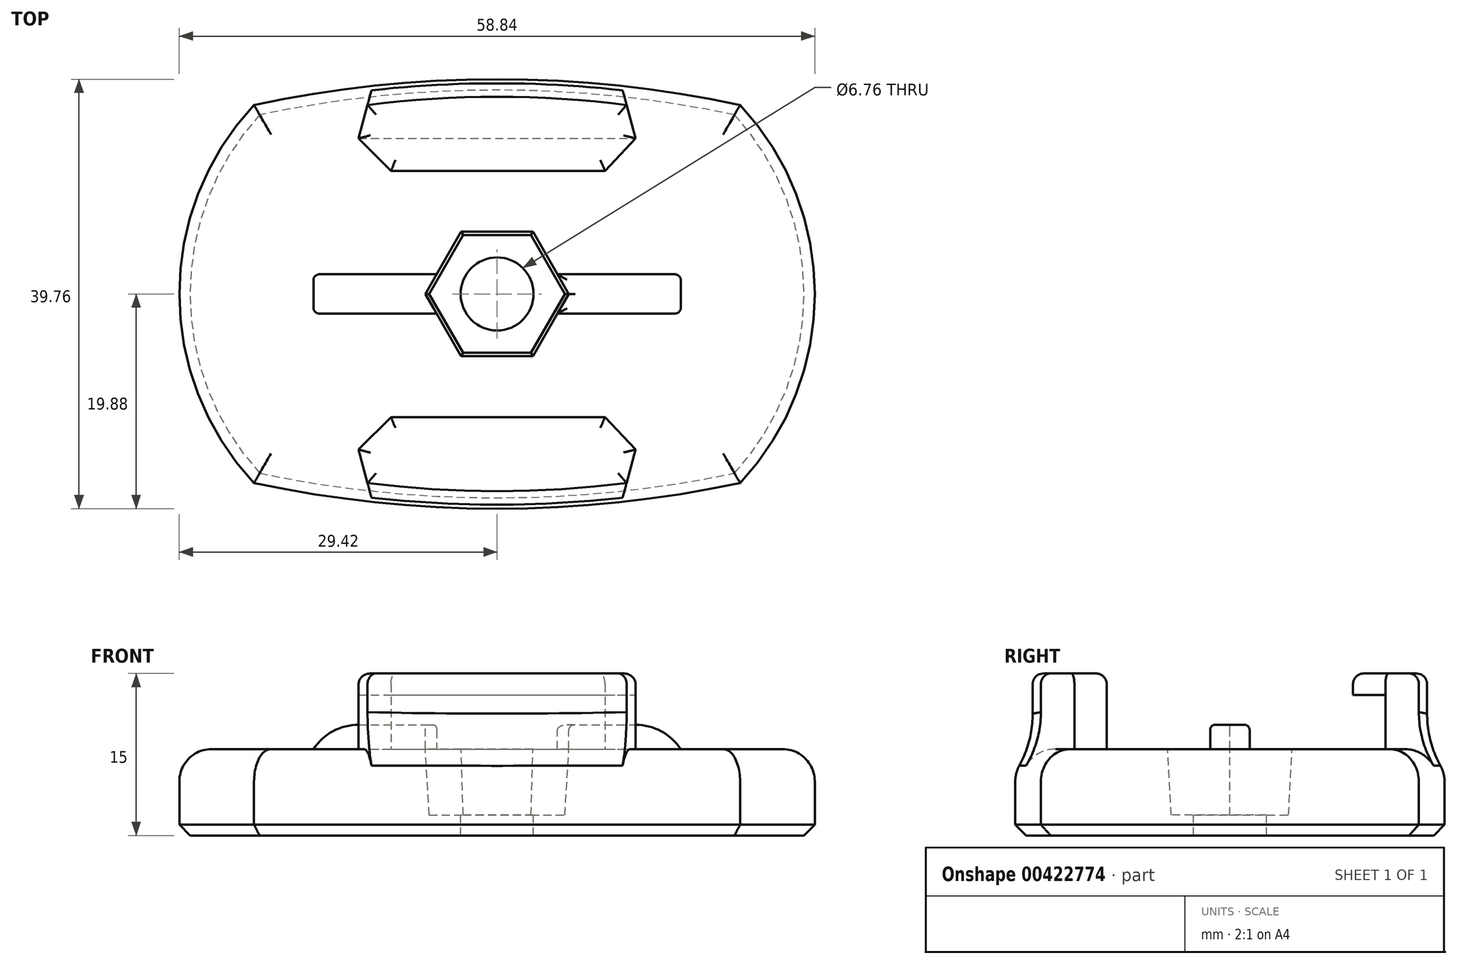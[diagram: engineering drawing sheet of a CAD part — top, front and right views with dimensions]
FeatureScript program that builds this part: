
annotation { "Feature Type Name" : "Feature", "Feature Type Description" : "" }
export const myFeature = defineFeature(function(context is Context, id is Id, definition is map)
    precondition{}
    {
        {
            var Q0;
            Q0=qCreatedBy(makeId("Top.planeOp"),FACE);
            var sketch = newSketch(context, id + "F0", { "sketchPlane" : qUnion([Q0])});
            skLineSegment(sketch, "E0.rect.bottom", {"start": v(-22.5, 17.5) * mm, "end": v(22.5, 17.5) * mm});
            skLineSegment(sketch, "E0.rect.top", {"start": v(-22.5, -17.5) * mm, "end": v(22.5, -17.5) * mm});
            skLineSegment(sketch, "E0.rect.left", {"start": v(-22.5, 17.5) * mm, "end": v(-22.5, -17.5) * mm});
            skLineSegment(sketch, "E0.rect.right", {"start": v(22.5, 17.5) * mm, "end": v(22.5, -17.5) * mm});
            skPoint(sketch, "E0.rect.middle", {"position": v(0, 0) * mm});
            skArc(sketch, "E1", {"start": v(-22.5, 17.5) * mm, "mid": v(-29.42, 0) * mm, "end": v(-22.5, -17.5) * mm});
            skArc(sketch, "E2.MirrorCS", {"start": v(22.5, 17.5) * mm, "mid": v(29.42, 0) * mm, "end": v(22.5, -17.5) * mm});
            skArc(sketch, "E3", {"start": v(22.5, 17.5) * mm, "mid": v(0, 19.88) * mm, "end": v(-22.5, 17.5) * mm});
            skArc(sketch, "E4.MirrorCS", {"start": v(22.5, -17.5) * mm, "mid": v(0, -19.88) * mm, "end": v(-22.5, -17.5) * mm});
            skSolve(sketch);
        }
        {
            var Q0;
            Q0=makeQuery(id+"F0.imprint","IMPRINT",FACE,{"disambiguationData":[TD([[makeQuery(id+"F0.imprint","IMPRINT",EDGE,{"derivedFrom":sQuery(id+"F0.wireOp",EDGE,"E0.rect.bottom")}),-1.0]])]});
            var Q1;
            Q1=makeQuery(id+"F0.imprint","IMPRINT",FACE,{"disambiguationData":[TD([[makeQuery(id+"F0.imprint","IMPRINT",EDGE,{"derivedFrom":sQuery(id+"F0.wireOp",EDGE,"E0.rect.left")}),-1.0]])]});
            var Q2;
            Q2=makeQuery(id+"F0.imprint","IMPRINT",FACE,{"disambiguationData":[TD([[makeQuery(id+"F0.imprint","IMPRINT",EDGE,{"derivedFrom":sQuery(id+"F0.wireOp",EDGE,"E0.rect.right")}),1.0]])]});
            var Q3;
            Q3=makeQuery(id+"F0.imprint","IMPRINT",FACE,{"disambiguationData":[TD([[makeQuery(id+"F0.imprint","IMPRINT",EDGE,{"derivedFrom":sQuery(id+"F0.wireOp",EDGE,"E0.rect.bottom")}),1.0]])]});
            var Q4;
            Q4=makeQuery(id+"F0.imprint","IMPRINT",FACE,{"disambiguationData":[TD([[makeQuery(id+"F0.imprint","IMPRINT",EDGE,{"derivedFrom":sQuery(id+"F0.wireOp",EDGE,"E0.rect.top")}),-1.0]])]});
            extrude(context, id + "F1", {"entities" : qUnion([Q0, Q1, Q2, Q3, Q4]), "depth" : 8 * mm});
        }
        {
            var Q0;
            Q0=makeQuery(id+"F1.opExtrude","CAP_FACE",FACE,{"disambiguationData":[OSD([sQuery(id+"F0.wireOp",EDGE,"E1"),sQuery(id+"F0.wireOp",EDGE,"E2.MirrorCS"),sQuery(id+"F0.wireOp",EDGE,"E3"),sQuery(id+"F0.wireOp",EDGE,"E4.MirrorCS")])],"isStart":false});
            var sketch = newSketch(context, id + "F2", { "sketchPlane" : qUnion([Q0])});
            skLineSegment(sketch, "E5.rect.bottom", {"start": v(-17, 1.82) * mm, "end": v(17, 1.82) * mm});
            skLineSegment(sketch, "E5.rect.top", {"start": v(-17, -1.83) * mm, "end": v(17, -1.83) * mm});
            skLineSegment(sketch, "E5.rect.left", {"start": v(-17, 1.82) * mm, "end": v(-17, -1.83) * mm});
            skLineSegment(sketch, "E5.rect.right", {"start": v(17, 1.82) * mm, "end": v(17, -1.83) * mm});
            skPoint(sketch, "E5.rect.middle", {"position": v(0, 0) * mm});
            skSolve(sketch);
        }
        {
            var Q0;
            Q0=makeQuery(id+"F2.imprint","IMPRINT",FACE,{"disambiguationData":[TD([[makeQuery(id+"F2.imprint","IMPRINT",EDGE,{"derivedFrom":sQuery(id+"F2.wireOp",EDGE,"E5.rect.bottom")}),-1.0]])]});
            extrude(context, id + "F3", {"entities" : qUnion([Q0]), "operationType" : NewBodyOperationType.ADD, "depth" : 2.25 * mm});
        }
        {
            var Q0;
            Q0=makeQuery(id+"F3.opExtrude","SWEPT_FACE",FACE,{"disambiguationData":[OSD([sQuery(id+"F2.wireOp",EDGE,"E5.rect.top")])]});
            var sketch = newSketch(context, id + "F4", { "sketchPlane" : qUnion([Q0])});
            skLineSegment(sketch, "E6", {"start": v(-17, 10.25) * mm, "end": v(17, 10.25) * mm, "construction": true});
            skLineSegment(sketch, "E7.0", {"start": v(-17, 9.25) * mm, "end": v(17, 9.25) * mm});
            skArc(sketch, "E8", {"start": v(-13.26, 10.25) * mm, "mid": v(-15.2, 10) * mm, "end": v(-17, 9.25) * mm});
            skLineSegment(sketch, "E9", {"start": v(0, 0) * mm, "end": v(0, 15.47) * mm, "construction": true});
            skArc(sketch, "E10.0.MirrorCS", {"start": v(13.26, 10.25) * mm, "mid": v(15.2, 10) * mm, "end": v(17, 9.25) * mm});
            skLineSegment(sketch, "E11", {"start": v(-17, 9.25) * mm, "end": v(-18.16, 9.25) * mm});
            skLineSegment(sketch, "E12", {"start": v(-18.16, 9.25) * mm, "end": v(-18.16, 11.7) * mm});
            skLineSegment(sketch, "E13", {"start": v(-18.16, 11.7) * mm, "end": v(-13.25, 11.7) * mm});
            skLineSegment(sketch, "E14", {"start": v(-13.25, 11.7) * mm, "end": v(-13.26, 10.25) * mm});
            skLineSegment(sketch, "E15", {"start": v(13.26, 10.25) * mm, "end": v(13.26, 11.4) * mm});
            skLineSegment(sketch, "E16", {"start": v(13.26, 11.4) * mm, "end": v(18.11, 11.4) * mm});
            skLineSegment(sketch, "E17", {"start": v(18.11, 11.4) * mm, "end": v(18.11, 9.28) * mm});
            skLineSegment(sketch, "E18", {"start": v(18.11, 9.28) * mm, "end": v(17, 9.25) * mm});
            skSolve(sketch);
        }
        {
            var Q0;
            Q0=makeQuery(id+"F1.opExtrude","CAP_FACE",FACE,{"disambiguationData":[OSD([sQuery(id+"F0.wireOp",EDGE,"E1"),sQuery(id+"F0.wireOp",EDGE,"E2.MirrorCS"),sQuery(id+"F0.wireOp",EDGE,"E3"),sQuery(id+"F0.wireOp",EDGE,"E4.MirrorCS")])],"isStart":false});
            var sketch = newSketch(context, id + "F5", { "sketchPlane" : qUnion([Q0])});
            skLineSegment(sketch, "E19.rect.bottom", {"start": v(-12, 17.5) * mm, "end": v(12, 17.5) * mm, "construction": true});
            skPoint(sketch, "E19.rect.middle", {"position": v(0, 0) * mm});
            skLineSegment(sketch, "E20.0", {"start": v(-9.82, 11.4) * mm, "end": v(10, 11.4) * mm});
            skLineSegment(sketch, "E21", {"start": v(-9.82, 11.4) * mm, "end": v(-12.82, 14.4) * mm, "construction": true});
            skLineSegment(sketch, "E22", {"start": v(-9.82, 11.4) * mm, "end": v(-12.83, 14.4) * mm, "construction": true});
            skLineSegment(sketch, "E23.0.MirrorCS", {"start": v(10, 11.4) * mm, "end": v(12.82, 14.4) * mm, "construction": true});
            skLineSegment(sketch, "E24", {"start": v(10, 11.4) * mm, "end": v(12.82, 14.4) * mm});
            skLineSegment(sketch, "E25", {"start": v(12, 17.5) * mm, "end": v(-12, 17.5) * mm});
            skLineSegment(sketch, "E26", {"start": v(-12.83, 14.4) * mm, "end": v(-9.82, 11.4) * mm});
            skLineSegment(sketch, "E27", {"start": v(12.83, 14.4) * mm, "end": v(12, 17.5) * mm});
            skLineSegment(sketch, "E28.0.MirrorCS", {"start": v(-12.83, 14.4) * mm, "end": v(-12, 17.5) * mm});
            skArc(sketch, "E29", {"start": v(12, 17.5) * mm, "mid": v(0, 18.26) * mm, "end": v(-12, 17.5) * mm});
            skLineSegment(sketch, "E30.MirrorCS", {"start": v(12, -17.5) * mm, "end": v(-12, -17.5) * mm});
            skLineSegment(sketch, "E31.MirrorCS", {"start": v(-12.83, -14.4) * mm, "end": v(-9.82, -11.4) * mm});
            skLineSegment(sketch, "E32.MirrorCS", {"start": v(-9.82, -11.4) * mm, "end": v(-12.82, -14.4) * mm, "construction": true});
            skLineSegment(sketch, "E33.MirrorCS", {"start": v(10, -11.4) * mm, "end": v(12.82, -14.4) * mm});
            skLineSegment(sketch, "E34.MirrorCS", {"start": v(-12, -17.5) * mm, "end": v(12, -17.5) * mm, "construction": true});
            skLineSegment(sketch, "E35.MirrorCS", {"start": v(-9.82, -11.4) * mm, "end": v(-12.83, -14.4) * mm, "construction": true});
            skLineSegment(sketch, "E36.MirrorCS", {"start": v(10, -11.4) * mm, "end": v(12.82, -14.4) * mm, "construction": true});
            skLineSegment(sketch, "E37.MirrorCS", {"start": v(-12.83, -14.4) * mm, "end": v(-12, -17.5) * mm});
            skLineSegment(sketch, "E38.MirrorCS", {"start": v(12.83, -14.4) * mm, "end": v(12, -17.5) * mm});
            skLineSegment(sketch, "E39.MirrorCS", {"start": v(-9.82, -11.4) * mm, "end": v(10, -11.4) * mm});
            skArc(sketch, "E40.MirrorCS", {"start": v(12, -17.5) * mm, "mid": v(0, -18.26) * mm, "end": v(-12, -17.5) * mm});
            skSolve(sketch);
        }
        {
            var Q0;
            Q0=qSketchRegion(id+"F5",true);
            extrude(context, id + "F6", {"entities" : qUnion([Q0]), "operationType" : NewBodyOperationType.ADD, "depth" : 7 * mm});
        }
        {
            var Q0;
            Q0=qCreatedBy(makeId("Right.planeOp"),FACE);
            var sketch = newSketch(context, id + "F7", { "sketchPlane" : qUnion([Q0])});
            skLineSegment(sketch, "E41.0", {"start": v(14.4, 13) * mm, "end": v(14.4, 8) * mm});
            skLineSegment(sketch, "E42.bottom", {"start": v(14.4, 8) * mm, "end": v(10.15, 8) * mm});
            skLineSegment(sketch, "E42.top", {"start": v(14.4, 13) * mm, "end": v(10.15, 13) * mm});
            skLineSegment(sketch, "E42.left", {"start": v(14.4, 8) * mm, "end": v(14.4, 13) * mm});
            skLineSegment(sketch, "E42.right", {"start": v(10.15, 8) * mm, "end": v(10.15, 13) * mm});
            skLineSegment(sketch, "E43.0.MirrorCS", {"start": v(-14.4, 8) * mm, "end": v(-14.4, 13) * mm});
            skLineSegment(sketch, "E43.1.MirrorCS", {"start": v(-14.4, 13) * mm, "end": v(-14.4, 8) * mm});
            skLineSegment(sketch, "E43.2.MirrorCS", {"start": v(-14.4, 13) * mm, "end": v(-10.15, 13) * mm});
            skLineSegment(sketch, "E43.3.MirrorCS", {"start": v(-10.15, 8) * mm, "end": v(-10.15, 13) * mm});
            skLineSegment(sketch, "E43.4.MirrorCS", {"start": v(-14.4, 8) * mm, "end": v(-10.15, 8) * mm});
            skSolve(sketch);
        }
        {
            var Q0;
            Q0=makeQuery(id+"F7.imprint","IMPRINT",FACE,{"disambiguationData":[TD([[makeQuery(id+"F7.imprint","IMPRINT",EDGE,{"derivedFrom":sQuery(id+"F7.wireOp",EDGE,"E42.bottom")}),-1.0]])]});
            var Q1;
            Q1=makeQuery(id+"F7.imprint","IMPRINT",FACE,{"disambiguationData":[TD([[makeQuery(id+"F7.imprint","IMPRINT",EDGE,{"derivedFrom":sQuery(id+"F7.wireOp",EDGE,"E43.1.MirrorCS")}),1.0]])]});
            extrude(context, id + "F8", {"entities" : qUnion([Q0, Q1]), "operationType" : NewBodyOperationType.REMOVE, "endBound" : BoundingType.SYMMETRIC, "oppositeDirection" : true, "depth" : 31.01 * mm});
        }
        {
            var Q0;
            Q0=makeQuery(id+"F1.opExtrude","CAP_EDGE",EDGE,{"disambiguationData":[OSD([sQuery(id+"F0.wireOp",EDGE,"E3")])],"isStart":false});
            var Q1;
            Q1=makeQuery(id+"F1.opExtrude","CAP_EDGE",EDGE,{"disambiguationData":[OSD([sQuery(id+"F0.wireOp",EDGE,"E1")])],"isStart":false});
            var Q2;
            Q2=makeQuery(id+"F1.opExtrude","CAP_EDGE",EDGE,{"disambiguationData":[OSD([sQuery(id+"F0.wireOp",EDGE,"E4.MirrorCS")])],"isStart":false});
            var Q3;
            Q3=makeQuery(id+"F1.opExtrude","CAP_EDGE",EDGE,{"disambiguationData":[OSD([sQuery(id+"F0.wireOp",EDGE,"E2.MirrorCS")])],"isStart":false});
            fillet(context, id + "F9", {"entities" : qUnion([Q0, Q1, Q2, Q3]), "radius" : 3 * mm, "tangentPropagation" : true, "allowEdgeOverflow" : false});
        }
        {
            var Q0;
            Q0=makeQuery(id+"F9.opFillet","BLEND_EDGE",EDGE,{"blendedFrom":[makeQuery(id+"F1.opExtrude","CAP_EDGE",EDGE,{"disambiguationData":[OSD([sQuery(id+"F0.wireOp",EDGE,"E4.MirrorCS")])],"isStart":false}),makeQuery(id+"F6.opExtrude","SWEPT_FACE",FACE,{"disambiguationData":[OSD([sQuery(id+"F5.wireOp",EDGE,"E40.MirrorCS")])]})],"blendedInto":[makeQuery(id+"F6.opExtrude","SWEPT_FACE",FACE,{"disambiguationData":[OSD([sQuery(id+"F5.wireOp",EDGE,"E40.MirrorCS")])]})]});
            var Q1;
            Q1=makeQuery(id+"F9.opFillet","BLEND_EDGE",EDGE,{"blendedFrom":[makeQuery(id+"F1.opExtrude","CAP_EDGE",EDGE,{"disambiguationData":[OSD([sQuery(id+"F0.wireOp",EDGE,"E3")])],"isStart":false}),makeQuery(id+"F6.opExtrude","SWEPT_FACE",FACE,{"disambiguationData":[OSD([sQuery(id+"F5.wireOp",EDGE,"E29")])]})],"blendedInto":[makeQuery(id+"F6.opExtrude","SWEPT_FACE",FACE,{"disambiguationData":[OSD([sQuery(id+"F5.wireOp",EDGE,"E29")])]})]});
            fillet(context, id + "F10", {"entities" : qUnion([Q0, Q1]), "radius" : 10 * mm, "tangentPropagation" : true, "allowEdgeOverflow" : false});
        }
        {
            var Q0;
            Q0=makeQuery(id+"F6.opExtrude","CAP_FACE",FACE,{"disambiguationData":[OSD([sQuery(id+"F5.wireOp",EDGE,"E31.MirrorCS"),sQuery(id+"F5.wireOp",EDGE,"E33.MirrorCS"),sQuery(id+"F5.wireOp",EDGE,"E37.MirrorCS"),sQuery(id+"F5.wireOp",EDGE,"E38.MirrorCS"),sQuery(id+"F5.wireOp",EDGE,"E39.MirrorCS"),sQuery(id+"F5.wireOp",EDGE,"E40.MirrorCS")])],"isStart":false});
            var Q1;
            Q1=makeQuery(id+"F6.opExtrude","CAP_FACE",FACE,{"disambiguationData":[OSD([sQuery(id+"F5.wireOp",EDGE,"E20.0"),sQuery(id+"F5.wireOp",EDGE,"E24"),sQuery(id+"F5.wireOp",EDGE,"E26"),sQuery(id+"F5.wireOp",EDGE,"E27"),sQuery(id+"F5.wireOp",EDGE,"E28.0.MirrorCS"),sQuery(id+"F5.wireOp",EDGE,"E29")])],"isStart":false});
            fillet(context, id + "F11", {"entities" : qUnion([Q0, Q1]), "radius" : 1 * mm, "tangentPropagation" : true, "allowEdgeOverflow" : false});
        }
        {
            var Q0;
            Q0=makeQuery(id+"F8.boolean.opBoolean","MERGE",FACE,{"derivedFrom":[makeQuery(id+"F1.opExtrude","CAP_FACE",FACE,{"disambiguationData":[OSD([sQuery(id+"F0.wireOp",EDGE,"E0.rect.bottom"),sQuery(id+"F0.wireOp",EDGE,"E0.rect.top"),sQuery(id+"F0.wireOp",EDGE,"E1"),sQuery(id+"F0.wireOp",EDGE,"E2.MirrorCS")])],"isStart":false}),makeQuery(id+"F8.opExtrude","SWEPT_FACE",FACE,{"disambiguationData":[OSD([sQuery(id+"F7.wireOp",EDGE,"E42.bottom")])]}),makeQuery(id+"F8.opExtrude","SWEPT_FACE",FACE,{"disambiguationData":[OSD([sQuery(id+"F7.wireOp",EDGE,"E43.4.MirrorCS")])]})]});
            var sketch = newSketch(context, id + "F12", { "sketchPlane" : qUnion([Q0])});
            skCircle(sketch, "E44.cCircle", {"center": v(0, 0) * mm, "radius": 5.76 * mm, "construction": true});
            skLineSegment(sketch, "E44.0", {"start": v(-3.32, -5.76) * mm, "end": v(-6.65, 0) * mm});
            skLineSegment(sketch, "E44.1", {"start": v(-6.65, 0) * mm, "end": v(-3.32, 5.76) * mm});
            skLineSegment(sketch, "E44.2", {"start": v(-3.32, 5.76) * mm, "end": v(3.32, 5.76) * mm});
            skLineSegment(sketch, "E44.3", {"start": v(3.32, 5.76) * mm, "end": v(6.65, 0) * mm});
            skLineSegment(sketch, "E44.4", {"start": v(6.65, 0) * mm, "end": v(3.32, -5.76) * mm});
            skLineSegment(sketch, "E44.5", {"start": v(3.32, -5.76) * mm, "end": v(-3.32, -5.76) * mm});
            skPoint(sketch, "E44.0.midPoint", {"position": v(-4.99, -2.88) * mm});
            skSolve(sketch);
        }
        {
            var Q0;
            Q0=qSketchRegion(id+"F12",true);
            var Q1;
            Q1=makeQuery(id+"F3.opExtrude","CAP_FACE",FACE,{"disambiguationData":[OSD([sQuery(id+"F2.wireOp",EDGE,"E5.rect.bottom"),sQuery(id+"F2.wireOp",EDGE,"E5.rect.top"),sQuery(id+"F2.wireOp",EDGE,"E5.rect.left"),sQuery(id+"F2.wireOp",EDGE,"E5.rect.right")])],"isStart":false});
            extrude(context, id + "F13", {"entities" : qUnion([Q0]), "operationType" : NewBodyOperationType.REMOVE, "oppositeDirection" : true, "depth" : (7 / 32) * 27.94 * mm, "hasDraft" : true, "draftAngle" : 3 * degree, "draftPullDirection" : true, "hasSecondDirection" : true, "secondDirectionBound" : SecondDirectionBoundingType.UP_TO_SURFACE, "secondDirectionOppositeDirection" : false, "secondDirectionBoundEntityFace" : qUnion([Q1]), "secondDirectionDepth" : 25 * mm});
        }
        {
            var Q0;
            Q0=sQuery(id+"F12.wireOp",VERTEX,"E44.cCircle.center");
            var Q1;
            Q1=makeQuery(id+"F1.opExtrude","SWEPT_BODY",BODY,{"disambiguationData":[OSD([sQuery(id+"F0.wireOp",EDGE,"E0.rect.bottom"),sQuery(id+"F0.wireOp",EDGE,"E0.rect.top"),sQuery(id+"F0.wireOp",EDGE,"E1"),sQuery(id+"F0.wireOp",EDGE,"E2.MirrorCS")])]});
            hole(context, id + "F14", {"style" : HoleStyle.SIMPLE, "endStyle" : HoleEndStyle.THROUGH, "standardTappedOrClearance" : lookupTablePath({ "standard" : "ANSI", "fit" : "Normal (ASME)", "size" : "1/4", "type" : "Clearance" }), "standardBlindInLast" : lookupTablePath({ "fit" : "Free", "standard" : "ANSI", "size" : "1/4", "type" : "Clearance" }), "holeDiameter" : 6.76 * mm, "tappedDepth" : 12 * mm, "tapClearance" : 3, "locations" : qUnion([Q0]), "scope" : qUnion([Q1])});
        }
        {
            var Q0;
            Q0=makeQuery(id+"F1.opExtrude","CAP_EDGE",EDGE,{"disambiguationData":[OSD([sQuery(id+"F0.wireOp",EDGE,"E0.rect.top")])],"isStart":true});
            var Q1;
            Q1=makeQuery(id+"F1.opExtrude","CAP_EDGE",EDGE,{"disambiguationData":[OSD([sQuery(id+"F0.wireOp",EDGE,"E2.MirrorCS")])],"isStart":true});
            var Q2;
            Q2=makeQuery(id+"F1.opExtrude","CAP_EDGE",EDGE,{"disambiguationData":[OSD([sQuery(id+"F0.wireOp",EDGE,"E0.rect.bottom")])],"isStart":true});
            var Q3;
            Q3=makeQuery(id+"F1.opExtrude","CAP_EDGE",EDGE,{"disambiguationData":[OSD([sQuery(id+"F0.wireOp",EDGE,"E1")])],"isStart":true});
            var Q4;
            Q4=makeQuery(id+"F1.opExtrude","CAP_EDGE",EDGE,{"disambiguationData":[OSD([sQuery(id+"F0.wireOp",EDGE,"E3")])],"isStart":true});
            var Q5;
            Q5=makeQuery(id+"F1.opExtrude","CAP_EDGE",EDGE,{"disambiguationData":[OSD([sQuery(id+"F0.wireOp",EDGE,"E4.MirrorCS")])],"isStart":true});
            chamfer(context, id + "F15", {"entities" : qUnion([Q0, Q1, Q2, Q3, Q4, Q5]), "width" : 1 * mm, "tangentPropagation" : true});
        }
        {
            var Q0;
            Q0=makeQuery(id+"F3.opExtrude","CAP_EDGE",EDGE,{"disambiguationData":[OSD([sQuery(id+"F2.wireOp",EDGE,"E5.rect.right")])],"isStart":false});
            var Q1;
            Q1=makeQuery(id+"F3.opExtrude","CAP_EDGE",EDGE,{"disambiguationData":[OSD([sQuery(id+"F2.wireOp",EDGE,"E5.rect.left")])],"isStart":false});
            fillet(context, id + "F16", {"entities" : qUnion([Q0, Q1]), "radius" : 5 * mm, "tangentPropagation" : true, "allowEdgeOverflow" : false});
        }
        {
            var Q0;
            {var subQ0=sQuery(id+"F2.wireOp",EDGE,"E5.rect.right");var subQ1=sQuery(id+"F2.wireOp",EDGE,"E5.rect.top");Q0=makeQuery(id+"F13.boolean.opBoolean","SPLIT",EDGE,{"disambiguationData":[TD([makeQuery(id+"F3.opExtrude","SWEPT_FACE",FACE,{"disambiguationData":[OSD([subQ0])]})])],"derivedFrom":makeQuery(id+"F3.opExtrude","CAP_EDGE",EDGE,{"disambiguationData":[OSD([subQ1])],"isStart":false})});}
            var Q1;
            {var subQ0=sQuery(id+"F2.wireOp",EDGE,"E5.rect.bottom");var subQ1=sQuery(id+"F2.wireOp",EDGE,"E5.rect.right");Q1=makeQuery(id+"F13.boolean.opBoolean","SPLIT",EDGE,{"disambiguationData":[TD([makeQuery(id+"F3.opExtrude","SWEPT_FACE",FACE,{"disambiguationData":[OSD([subQ1])]})])],"derivedFrom":makeQuery(id+"F3.opExtrude","CAP_EDGE",EDGE,{"disambiguationData":[OSD([subQ0])],"isStart":false})});}
            var Q2;
            {var subQ0=sQuery(id+"F2.wireOp",EDGE,"E5.rect.bottom");var subQ1=sQuery(id+"F2.wireOp",EDGE,"E5.rect.left");Q2=makeQuery(id+"F13.boolean.opBoolean","SPLIT",EDGE,{"disambiguationData":[TD([makeQuery(id+"F3.opExtrude","SWEPT_FACE",FACE,{"disambiguationData":[OSD([subQ1])]})])],"derivedFrom":makeQuery(id+"F3.opExtrude","CAP_EDGE",EDGE,{"disambiguationData":[OSD([subQ0])],"isStart":false})});}
            var Q3;
            {var subQ0=sQuery(id+"F2.wireOp",EDGE,"E5.rect.left");var subQ1=sQuery(id+"F2.wireOp",EDGE,"E5.rect.top");Q3=makeQuery(id+"F13.boolean.opBoolean","SPLIT",EDGE,{"disambiguationData":[TD([makeQuery(id+"F3.opExtrude","SWEPT_FACE",FACE,{"disambiguationData":[OSD([subQ0])]})])],"derivedFrom":makeQuery(id+"F3.opExtrude","CAP_EDGE",EDGE,{"disambiguationData":[OSD([subQ1])],"isStart":false})});}
            var Q4;
            Q4=makeQuery(id+"F13.boolean.opBoolean","COPY",EDGE,{"derivedFrom":makeQuery(id+"F13.opExtrude","CAP_EDGE",EDGE,{"disambiguationData":[OSD([sQuery(id+"F12.wireOp",EDGE,"E44.1")])],"isStart":true})});
            var Q5;
            Q5=makeQuery(id+"F13.boolean.opBoolean","COPY",EDGE,{"derivedFrom":makeQuery(id+"F13.opExtrude","CAP_EDGE",EDGE,{"disambiguationData":[OSD([sQuery(id+"F12.wireOp",EDGE,"E44.0")])],"isStart":true})});
            var Q6;
            Q6=makeQuery(id+"F13.boolean.opBoolean","COPY",EDGE,{"derivedFrom":makeQuery(id+"F13.opExtrude","CAP_EDGE",EDGE,{"disambiguationData":[OSD([sQuery(id+"F12.wireOp",EDGE,"E44.4")])],"isStart":true})});
            var Q7;
            Q7=makeQuery(id+"F13.boolean.opBoolean","COPY",EDGE,{"derivedFrom":makeQuery(id+"F13.opExtrude","CAP_EDGE",EDGE,{"disambiguationData":[OSD([sQuery(id+"F12.wireOp",EDGE,"E44.3")])],"isStart":true})});
            fillet(context, id + "F17", {"entities" : qUnion([Q0, Q1, Q2, Q3, Q4, Q5, Q6, Q7]), "radius" : .5 * mm, "tangentPropagation" : true, "allowEdgeOverflow" : false});
        }
    });
